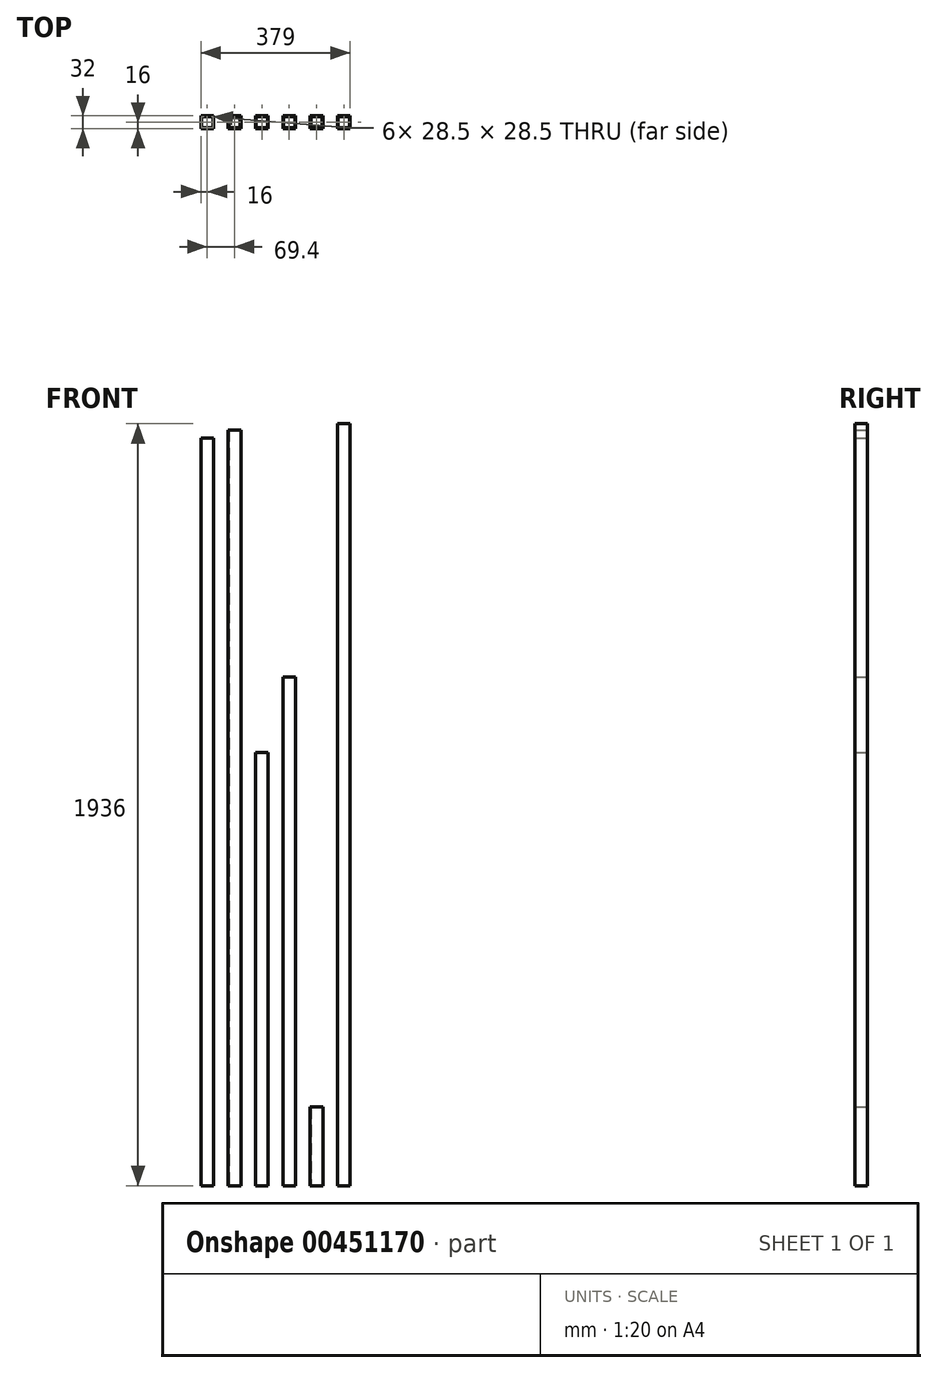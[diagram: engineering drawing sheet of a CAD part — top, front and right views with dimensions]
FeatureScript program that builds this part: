
annotation { "Feature Type Name" : "Feature", "Feature Type Description" : "" }
export const myFeature = defineFeature(function(context is Context, id is Id, definition is map)
    precondition{}
    {
        {
            var Q0;
            Q0=qCreatedBy(makeId("Top.planeOp"),FACE);
            var sketch = newSketch(context, id + "F0", { "sketchPlane" : qUnion([Q0])});
            skLineSegment(sketch, "E0.bottom", {"start": v(16, -16) * mm, "end": v(-16, -16) * mm});
            skLineSegment(sketch, "E0.top", {"start": v(16, 16) * mm, "end": v(-16, 16) * mm});
            skLineSegment(sketch, "E0.left", {"start": v(16, -16) * mm, "end": v(16, 16) * mm});
            skLineSegment(sketch, "E0.right", {"start": v(-16, -16) * mm, "end": v(-16, 16) * mm});
            skPoint(sketch, "E0.middle", {"position": v(0, 0) * mm});
            skLineSegment(sketch, "E1.bottom", {"start": v(14.25, -14.25) * mm, "end": v(-14.25, -14.25) * mm});
            skLineSegment(sketch, "E1.top", {"start": v(14.25, 14.25) * mm, "end": v(-14.25, 14.25) * mm});
            skLineSegment(sketch, "E1.left", {"start": v(14.25, -14.25) * mm, "end": v(14.25, 14.25) * mm});
            skLineSegment(sketch, "E1.right", {"start": v(-14.25, -14.25) * mm, "end": v(-14.25, 14.25) * mm});
            skLineSegment(sketch, "E2.1.0.0", {"start": v(55.15, -14.25) * mm, "end": v(55.15, 14.25) * mm});
            skLineSegment(sketch, "E2.1.0.1", {"start": v(85.4, -16) * mm, "end": v(85.4, 16) * mm});
            skLineSegment(sketch, "E2.1.0.2", {"start": v(83.65, -14.25) * mm, "end": v(83.65, 14.25) * mm});
            skPoint(sketch, "E2.1.0.3", {"position": v(69.4, 0) * mm});
            skLineSegment(sketch, "E2.1.0.4", {"start": v(83.65, 14.25) * mm, "end": v(55.15, 14.25) * mm});
            skLineSegment(sketch, "E2.1.0.5", {"start": v(53.4, -16) * mm, "end": v(53.4, 16) * mm});
            skLineSegment(sketch, "E2.1.0.6", {"start": v(85.4, -16) * mm, "end": v(53.4, -16) * mm});
            skLineSegment(sketch, "E2.1.0.7", {"start": v(83.65, -14.25) * mm, "end": v(55.15, -14.25) * mm});
            skLineSegment(sketch, "E2.1.0.8", {"start": v(85.4, 16) * mm, "end": v(53.4, 16) * mm});
            skPoint(sketch, "E2.1.0.9", {"position": v(69.4, 0) * mm});
            skLineSegment(sketch, "E2.2.0.0", {"start": v(124.55, -14.25) * mm, "end": v(124.55, 14.25) * mm});
            skLineSegment(sketch, "E2.2.0.1", {"start": v(154.8, -16) * mm, "end": v(154.8, 16) * mm});
            skLineSegment(sketch, "E2.2.0.2", {"start": v(153.05, -14.25) * mm, "end": v(153.05, 14.25) * mm});
            skPoint(sketch, "E2.2.0.3", {"position": v(138.8, 0) * mm});
            skLineSegment(sketch, "E2.2.0.4", {"start": v(153.05, 14.25) * mm, "end": v(124.55, 14.25) * mm});
            skLineSegment(sketch, "E2.2.0.5", {"start": v(122.8, -16) * mm, "end": v(122.8, 16) * mm});
            skLineSegment(sketch, "E2.2.0.6", {"start": v(154.8, -16) * mm, "end": v(122.8, -16) * mm});
            skLineSegment(sketch, "E2.2.0.7", {"start": v(153.05, -14.25) * mm, "end": v(124.55, -14.25) * mm});
            skLineSegment(sketch, "E2.2.0.8", {"start": v(154.8, 16) * mm, "end": v(122.8, 16) * mm});
            skPoint(sketch, "E2.2.0.9", {"position": v(138.8, 0) * mm});
            skLineSegment(sketch, "E2.direction1", {"start": v(-16, -16) * mm, "end": v(53.4, -16) * mm, "construction": true});
            skLineSegment(sketch, "E3.0.3.0", {"start": v(193.95, -14.25) * mm, "end": v(193.95, 14.25) * mm});
            skLineSegment(sketch, "E3.3.3.0", {"start": v(224.2, -16) * mm, "end": v(224.2, 16) * mm});
            skLineSegment(sketch, "E3.6.3.0", {"start": v(222.45, -14.25) * mm, "end": v(222.45, 14.25) * mm});
            skPoint(sketch, "E3.9.3.0", {"position": v(208.2, 0) * mm});
            skLineSegment(sketch, "E3.10.3.0", {"start": v(222.45, 14.25) * mm, "end": v(193.95, 14.25) * mm});
            skLineSegment(sketch, "E3.13.3.0", {"start": v(192.2, -16) * mm, "end": v(192.2, 16) * mm});
            skLineSegment(sketch, "E3.16.3.0", {"start": v(224.2, -16) * mm, "end": v(192.2, -16) * mm});
            skLineSegment(sketch, "E3.19.3.0", {"start": v(222.45, -14.25) * mm, "end": v(193.95, -14.25) * mm});
            skLineSegment(sketch, "E3.22.3.0", {"start": v(224.2, 16) * mm, "end": v(192.2, 16) * mm});
            skPoint(sketch, "E3.25.3.0", {"position": v(208.2, 0) * mm});
            skLineSegment(sketch, "E3.0.4.0", {"start": v(263.35, -14.25) * mm, "end": v(263.35, 14.25) * mm});
            skLineSegment(sketch, "E3.3.4.0", {"start": v(293.6, -16) * mm, "end": v(293.6, 16) * mm});
            skLineSegment(sketch, "E3.6.4.0", {"start": v(291.85, -14.25) * mm, "end": v(291.85, 14.25) * mm});
            skPoint(sketch, "E3.9.4.0", {"position": v(277.6, 0) * mm});
            skLineSegment(sketch, "E3.10.4.0", {"start": v(291.85, 14.25) * mm, "end": v(263.35, 14.25) * mm});
            skLineSegment(sketch, "E3.13.4.0", {"start": v(261.6, -16) * mm, "end": v(261.6, 16) * mm});
            skLineSegment(sketch, "E3.16.4.0", {"start": v(293.6, -16) * mm, "end": v(261.6, -16) * mm});
            skLineSegment(sketch, "E3.19.4.0", {"start": v(291.85, -14.25) * mm, "end": v(263.35, -14.25) * mm});
            skLineSegment(sketch, "E3.22.4.0", {"start": v(293.6, 16) * mm, "end": v(261.6, 16) * mm});
            skPoint(sketch, "E3.25.4.0", {"position": v(277.6, 0) * mm});
            skLineSegment(sketch, "E4.0.5.0", {"start": v(332.75, -14.25) * mm, "end": v(332.75, 14.25) * mm});
            skLineSegment(sketch, "E4.3.5.0", {"start": v(363, -16) * mm, "end": v(363, 16) * mm});
            skLineSegment(sketch, "E4.6.5.0", {"start": v(361.25, -14.25) * mm, "end": v(361.25, 14.25) * mm});
            skPoint(sketch, "E4.9.5.0", {"position": v(347, 0) * mm});
            skLineSegment(sketch, "E4.10.5.0", {"start": v(361.25, 14.25) * mm, "end": v(332.75, 14.25) * mm});
            skLineSegment(sketch, "E4.13.5.0", {"start": v(331, -16) * mm, "end": v(331, 16) * mm});
            skLineSegment(sketch, "E4.16.5.0", {"start": v(363, -16) * mm, "end": v(331, -16) * mm});
            skLineSegment(sketch, "E4.19.5.0", {"start": v(361.25, -14.25) * mm, "end": v(332.75, -14.25) * mm});
            skLineSegment(sketch, "E4.22.5.0", {"start": v(363, 16) * mm, "end": v(331, 16) * mm});
            skPoint(sketch, "E4.25.5.0", {"position": v(347, 0) * mm});
            skSolve(sketch);
        }
        {
            var Q0;
            Q0=makeQuery(id+"F0.imprint","IMPRINT",FACE,{"disambiguationData":[TD([[makeQuery(id+"F0.imprint","IMPRINT",EDGE,{"derivedFrom":sQuery(id+"F0.wireOp",EDGE,"E0.bottom")}),-1.0]])]});
            extrude(context, id + "F1", {"entities" : qUnion([Q0]), "depth" : 1900 * mm, "offsetDistance" : 25 * mm});
        }
        {
            var Q0;
            Q0=makeQuery(id+"F0.imprint","IMPRINT",FACE,{"disambiguationData":[TD([[makeQuery(id+"F0.imprint","IMPRINT",EDGE,{"derivedFrom":sQuery(id+"F0.wireOp",EDGE,"E2.1.0.0")}),1.0]])]});
            extrude(context, id + "F2", {"entities" : qUnion([Q0]), "depth" : 1920 * mm, "offsetDistance" : 25 * mm});
        }
        {
            var Q0;
            Q0=makeQuery(id+"F0.imprint","IMPRINT",FACE,{"disambiguationData":[TD([[makeQuery(id+"F0.imprint","IMPRINT",EDGE,{"derivedFrom":sQuery(id+"F0.wireOp",EDGE,"E2.2.0.0")}),1.0]])]});
            extrude(context, id + "F3", {"entities" : qUnion([Q0]), "depth" : 1100 * mm, "offsetDistance" : 25 * mm});
        }
        {
            var Q0;
            Q0=makeQuery(id+"F0.imprint","IMPRINT",FACE,{"disambiguationData":[TD([[makeQuery(id+"F0.imprint","IMPRINT",EDGE,{"derivedFrom":sQuery(id+"F0.wireOp",EDGE,"E3.0.3.0")}),1.0]])]});
            extrude(context, id + "F4", {"entities" : qUnion([Q0]), "depth" : 1292 * mm, "offsetDistance" : 25 * mm});
        }
        {
            var Q0;
            Q0=makeQuery(id+"F0.imprint","IMPRINT",FACE,{"disambiguationData":[TD([[makeQuery(id+"F0.imprint","IMPRINT",EDGE,{"derivedFrom":sQuery(id+"F0.wireOp",EDGE,"E3.0.4.0")}),1.0]])]});
            extrude(context, id + "F5", {"entities" : qUnion([Q0]), "depth" : 200 * mm, "offsetDistance" : 25 * mm});
        }
        {
            var Q0;
            Q0=makeQuery(id+"F0.imprint","IMPRINT",FACE,{"disambiguationData":[TD([[makeQuery(id+"F0.imprint","IMPRINT",EDGE,{"derivedFrom":sQuery(id+"F0.wireOp",EDGE,"E4.0.5.0")}),1.0]])]});
            extrude(context, id + "F6", {"entities" : qUnion([Q0]), "depth" : 1936 * mm, "offsetDistance" : 25 * mm});
        }
    });
